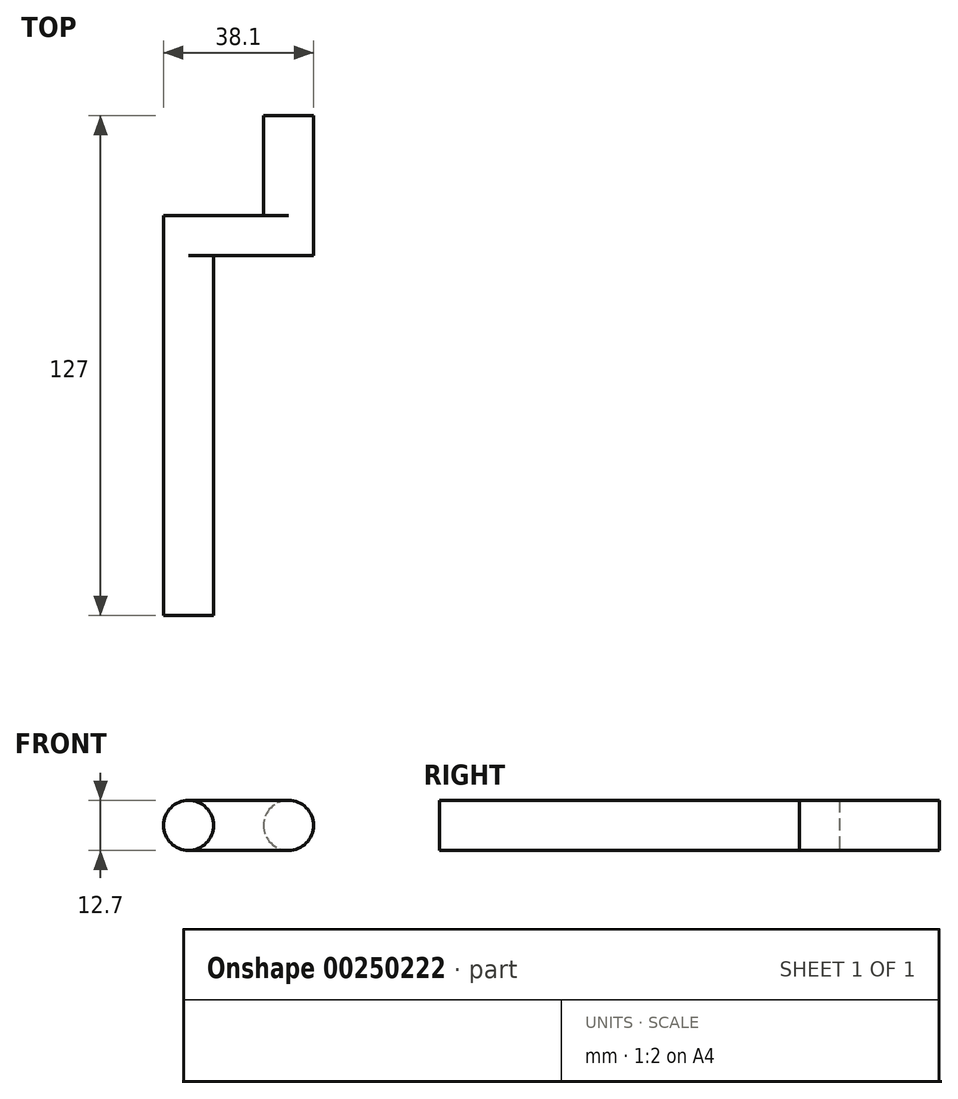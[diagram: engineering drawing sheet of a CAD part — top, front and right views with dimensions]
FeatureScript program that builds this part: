
annotation { "Feature Type Name" : "Feature", "Feature Type Description" : "" }
export const myFeature = defineFeature(function(context is Context, id is Id, definition is map)
    precondition{}
    {
        {
            var Q0;
            Q0=qCreatedBy(makeId("Front.planeOp"),FACE);
            var sketch = newSketch(context, id + "F0", { "sketchPlane" : qUnion([Q0])});
            skCircle(sketch, "E0", {"center": v(0, 0) * mm, "radius": 6.35 * mm});
            skSolve(sketch);
        }
        {
            var Q0;
            Q0=makeQuery(id+"F0.imprint","IMPRINT",FACE,{"disambiguationData":[TD([[makeQuery(id+"F0.imprint","IMPRINT",EDGE,{"derivedFrom":sQuery(id+"F0.wireOp",EDGE,"E0")}),1.0]])]});
            extrude(context, id + "F1", {"entities" : qUnion([Q0]), "depth" : 101.6 * mm});
        }
        {
            var Q0;
            Q0=makeQuery(id+"F1.opExtrude","CAP_FACE",FACE,{"disambiguationData":[OSD([sQuery(id+"F0.wireOp",EDGE,"E0")])],"isStart":true});
            var sketch = newSketch(context, id + "F2", { "sketchPlane" : qUnion([Q0])});
            skCircle(sketch, "E1", {"center": v(0, 0) * mm, "radius": 6.35 * mm});
            skLineSegment(sketch, "E2", {"start": v(0, 6.35) * mm, "end": v(-25.4, 6.35) * mm});
            skLineSegment(sketch, "E3", {"start": v(0, -6.35) * mm, "end": v(-25.4, -6.35) * mm});
            skLineSegment(sketch, "E4", {"start": v(-25.4, 6.35) * mm, "end": v(-25.4, -6.35) * mm});
            skCircle(sketch, "E5", {"center": v(-25.4, 0) * mm, "radius": 6.35 * mm});
            skSolve(sketch);
        }
        {
            var Q0;
            {var subQ0=sQuery(id+"F2.wireOp",EDGE,"E2");Q0=makeQuery(id+"F2.imprint","IMPRINT",FACE,{"disambiguationData":[TD([[makeQuery(id+"F2.imprint","IMPRINT",EDGE,{"derivedFrom":subQ0}),1.0]])]});}
            var Q1;
            {var subQ0=sQuery(id+"F2.wireOp",EDGE,"E4");Q1=makeQuery(id+"F2.imprint","IMPRINT",FACE,{"disambiguationData":[TD([[makeQuery(id+"F2.imprint","IMPRINT",EDGE,{"derivedFrom":subQ0}),-1.0]])]});}
            var Q2;
            {var subQ0=sQuery(id+"F2.wireOp",EDGE,"E4");Q2=makeQuery(id+"F2.imprint","IMPRINT",FACE,{"disambiguationData":[TD([[makeQuery(id+"F2.imprint","IMPRINT",EDGE,{"derivedFrom":subQ0}),1.0]])]});}
            extrude(context, id + "F3", {"entities" : qUnion([Q0, Q1, Q2]), "operationType" : NewBodyOperationType.ADD, "oppositeDirection" : true, "depth" : 10.16 * mm});
        }
        {
            var Q0;
            {var subQ0=sQuery(id+"F2.wireOp",EDGE,"E4");Q0=makeQuery(id+"F2.imprint","IMPRINT",FACE,{"disambiguationData":[TD([[makeQuery(id+"F2.imprint","IMPRINT",EDGE,{"derivedFrom":subQ0}),-1.0]])]});}
            var Q1;
            {var subQ0=sQuery(id+"F2.wireOp",EDGE,"E4");Q1=makeQuery(id+"F2.imprint","IMPRINT",FACE,{"disambiguationData":[TD([[makeQuery(id+"F2.imprint","IMPRINT",EDGE,{"derivedFrom":subQ0}),1.0]])]});}
            extrude(context, id + "F4", {"entities" : qUnion([Q0, Q1]), "operationType" : NewBodyOperationType.ADD, "depth" : 25.4 * mm});
        }
    });
